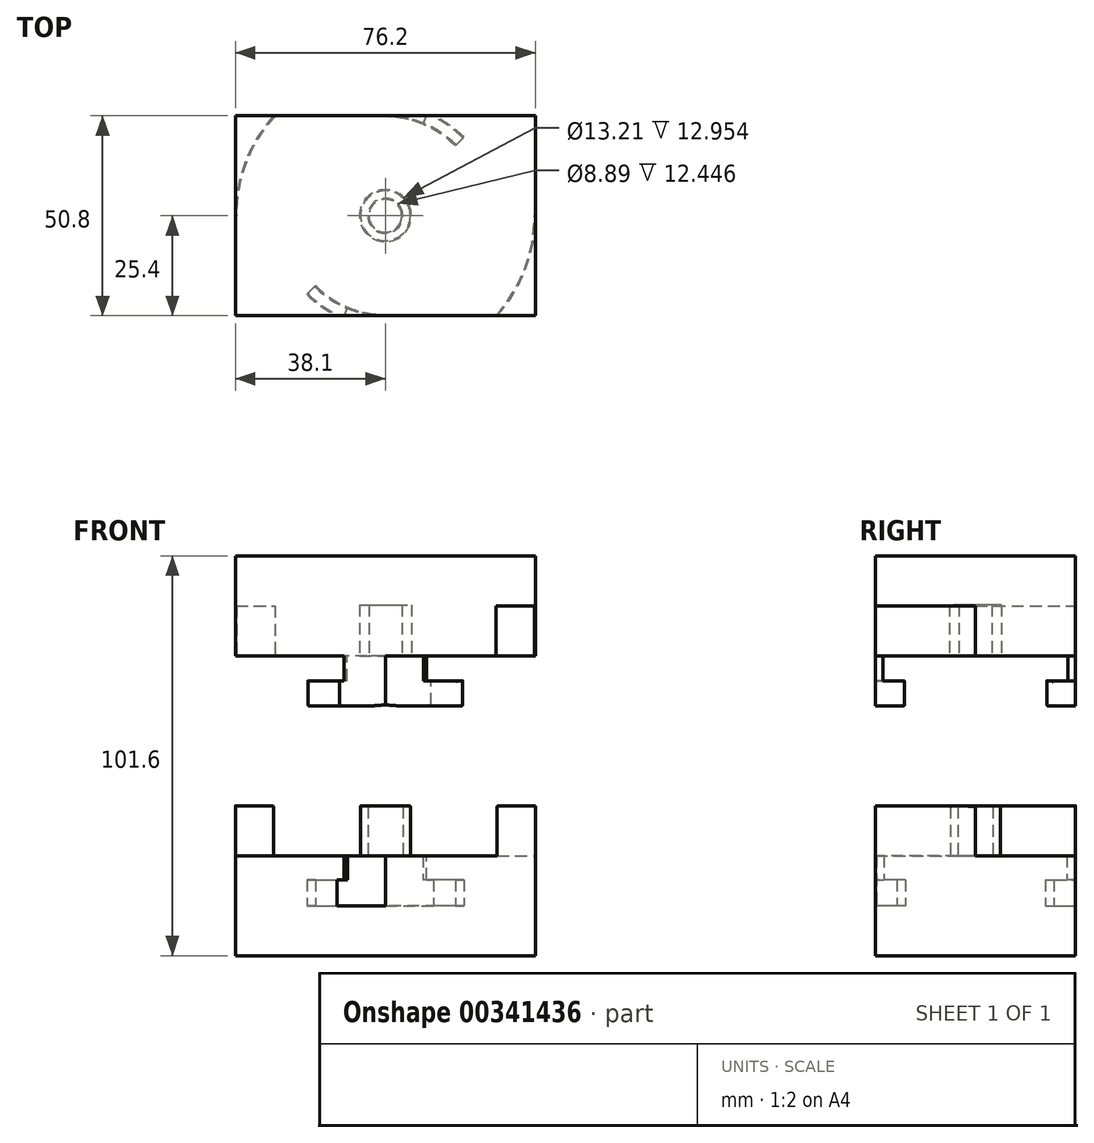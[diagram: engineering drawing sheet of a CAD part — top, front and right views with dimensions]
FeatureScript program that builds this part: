
annotation { "Feature Type Name" : "Feature", "Feature Type Description" : "" }
export const myFeature = defineFeature(function(context is Context, id is Id, definition is map)
    precondition{}
    {
        {
            var Q0;
            Q0=qCreatedBy(makeId("Top.planeOp"),FACE);
            var sketch = newSketch(context, id + "F0", { "sketchPlane" : qUnion([Q0])});
            skLineSegment(sketch, "E0.bottom", {"start": v(-38.1, 25.4) * mm, "end": v(38.1, 25.4) * mm});
            skLineSegment(sketch, "E0.top", {"start": v(-38.1, -25.4) * mm, "end": v(38.1, -25.4) * mm});
            skLineSegment(sketch, "E0.left", {"start": v(-38.1, 25.4) * mm, "end": v(-38.1, -25.4) * mm});
            skLineSegment(sketch, "E0.right", {"start": v(38.1, 25.4) * mm, "end": v(38.1, -25.4) * mm});
            skPoint(sketch, "E0.middle", {"position": v(0, 0) * mm});
            skSolve(sketch);
        }
        {
            var Q0;
            Q0=makeQuery(id+"F0.imprint","IMPRINT",FACE,{"disambiguationData":[TD([[makeQuery(id+"F0.imprint","IMPRINT",EDGE,{"derivedFrom":sQuery(id+"F0.wireOp",EDGE,"E0.bottom")}),-1.0]])]});
            extrude(context, id + "F1", {"entities" : qUnion([Q0]), "depth" : 25.4 * mm});
        }
        {
            var Q0;
            Q0=qCreatedBy(makeId("Top.planeOp"),FACE);
            cPlane(context, id + "F2", {"entities" : qUnion([Q0]), "cplaneType" : CPlaneType.OFFSET, "offset" : 101.6 * mm, "width" : 152.4 * mm, "height" : 152.4 * mm});
        }
        {
            var Q0;
            Q0=qCreatedBy(id+"F2.planeOp",FACE);
            var sketch = newSketch(context, id + "F3", { "sketchPlane" : qUnion([Q0])});
            skLineSegment(sketch, "E1.bottom", {"start": v(-38.1, -25.4) * mm, "end": v(38.1, -25.4) * mm});
            skLineSegment(sketch, "E1.top", {"start": v(-38.1, 25.4) * mm, "end": v(38.1, 25.4) * mm});
            skLineSegment(sketch, "E1.left", {"start": v(-38.1, -25.4) * mm, "end": v(-38.1, 25.4) * mm});
            skLineSegment(sketch, "E1.right", {"start": v(38.1, -25.4) * mm, "end": v(38.1, 25.4) * mm});
            skPoint(sketch, "E1.middle", {"position": v(0, 0) * mm});
            skSolve(sketch);
        }
        {
            var Q0;
            Q0=makeQuery(id+"F3.imprint","IMPRINT",FACE,{"disambiguationData":[TD([[makeQuery(id+"F3.imprint","IMPRINT",EDGE,{"derivedFrom":sQuery(id+"F3.wireOp",EDGE,"E1.bottom")}),1.0]])]});
            extrude(context, id + "F4", {"entities" : qUnion([Q0]), "oppositeDirection" : true, "depth" : 25.4 * mm});
        }
        {
            var Q0;
            Q0=makeQuery(id+"F1.opExtrude","CAP_FACE",FACE,{"disambiguationData":[OSD([sQuery(id+"F0.wireOp",EDGE,"E0.bottom"),sQuery(id+"F0.wireOp",EDGE,"E0.top"),sQuery(id+"F0.wireOp",EDGE,"E0.left"),sQuery(id+"F0.wireOp",EDGE,"E0.right")])],"isStart":false});
            var sketch = newSketch(context, id + "F5", { "sketchPlane" : qUnion([Q0])});
            skCircle(sketch, "E2", {"center": v(0, 0) * mm, "radius": 6.35 * mm});
            skCircle(sketch, "E3", {"center": v(0, 0) * mm, "radius": 4.45 * mm});
            skSolve(sketch);
        }
        {
            var Q0;
            Q0 = qSketchRegion(id + "F5", true);
            extrude(context, id + "F6", {"entities" : qUnion([Q0]), "operationType" : NewBodyOperationType.ADD, "depth" : 12.7 * mm});
        }
        {
            var Q0;
            Q0=makeQuery(id+"F4.opExtrude","CAP_FACE",FACE,{"disambiguationData":[OSD([sQuery(id+"F3.wireOp",EDGE,"E1.bottom"),sQuery(id+"F3.wireOp",EDGE,"E1.top"),sQuery(id+"F3.wireOp",EDGE,"E1.left"),sQuery(id+"F3.wireOp",EDGE,"E1.right")])],"isStart":false});
            var sketch = newSketch(context, id + "F7", { "sketchPlane" : qUnion([Q0])});
            skCircle(sketch, "E4", {"center": v(0, 0) * mm, "radius": 6.6 * mm});
            skCircle(sketch, "E5", {"center": v(0, 0) * mm, "radius": 4.2 * mm});
            skSolve(sketch);
        }
        {
            var Q0;
            Q0 = qSketchRegion(id + "F7", true);
            extrude(context, id + "F8", {"entities" : qUnion([Q0]), "operationType" : NewBodyOperationType.REMOVE, "oppositeDirection" : true, "depth" : 12.95 * mm});
        }
        {
            var Q0;
            Q0=makeQuery(id+"F8.boolean.opBoolean","COPY",EDGE,{"derivedFrom":makeQuery(id+"F8.opExtrude","CAP_EDGE",EDGE,{"disambiguationData":[OSD([sQuery(id+"F7.wireOp",EDGE,"E5")])],"isStart":true})});
            var Q1;
            Q1=makeQuery(id+"F8.boolean.opBoolean","COPY",EDGE,{"derivedFrom":makeQuery(id+"F8.opExtrude","CAP_EDGE",EDGE,{"disambiguationData":[OSD([sQuery(id+"F7.wireOp",EDGE,"E4")])],"isStart":true})});
            fillet(context, id + "F9", {"entities" : qUnion([Q0, Q1]), "radius" : 0.25 * mm, "tangentPropagation" : true, "allowEdgeOverflow" : false});
        }
        {
            var Q0;
            Q0=makeQuery(id+"F6.opExtrude","CAP_EDGE",EDGE,{"disambiguationData":[OSD([sQuery(id+"F5.wireOp",EDGE,"E2")])],"isStart":false});
            var Q1;
            Q1=makeQuery(id+"F6.opExtrude","CAP_EDGE",EDGE,{"disambiguationData":[OSD([sQuery(id+"F5.wireOp",EDGE,"E3")])],"isStart":false});
            fillet(context, id + "F10", {"entities" : qUnion([Q0, Q1]), "radius" : 0.25 * mm, "tangentPropagation" : true, "allowEdgeOverflow" : false});
        }
        {
            var Q0;
            {var subQ0=sQuery(id+"F3.wireOp",EDGE,"E1.left");var subQ1=sQuery(id+"F3.wireOp",EDGE,"E1.top");var subQ2=sQuery(id+"F3.wireOp",EDGE,"E1.right");var subQ3=sQuery(id+"F3.wireOp",EDGE,"E1.bottom");Q0=makeQuery(id+"F8.boolean.opBoolean","SPLIT",FACE,{"disambiguationData":[TD([makeQuery(id+"F4.opExtrude","SWEPT_FACE",FACE,{"disambiguationData":[OSD([subQ3])]})])],"derivedFrom":makeQuery(id+"F4.opExtrude","CAP_FACE",FACE,{"disambiguationData":[OSD([subQ3,subQ1,subQ0,subQ2])],"isStart":false})});}
            var sketch = newSketch(context, id + "F11", { "sketchPlane" : qUnion([Q0])});
            skCircle(sketch, "E6", {"center": v(0, 0) * mm, "radius": 25.4 * mm});
            skCircle(sketch, "E7", {"center": v(0, 0) * mm, "radius": 27.94 * mm});
            skLineSegment(sketch, "E8", {"start": v(-11.64, 25.4) * mm, "end": v(0, 25.4) * mm});
            skLineSegment(sketch, "E9", {"start": v(0, -25.4) * mm, "end": v(11.64, -25.4) * mm});
            skLineSegment(sketch, "E10", {"start": v(-25.4, 0) * mm, "end": v(-27.94, 0) * mm});
            skLineSegment(sketch, "E11", {"start": v(25.4, 0) * mm, "end": v(27.94, 0) * mm});
            skLineSegment(sketch, "E12.1.0", {"start": v(23.47, 9.72) * mm, "end": v(25.81, 10.7) * mm});
            skLineSegment(sketch, "E12.2.0", {"start": v(17.96, 17.96) * mm, "end": v(19.76, 19.76) * mm});
            skLineSegment(sketch, "E13.1.3.0", {"start": v(9.72, 23.47) * mm, "end": v(10.7, 25.81) * mm});
            skLineSegment(sketch, "E13.1.4.0", {"start": v(0, 25.4) * mm, "end": v(0, 27.94) * mm});
            skLineSegment(sketch, "E13.1.5.0", {"start": v(-9.72, 23.47) * mm, "end": v(-10.7, 25.81) * mm});
            skLineSegment(sketch, "E13.1.6.0", {"start": v(-17.96, 17.96) * mm, "end": v(-19.76, 19.76) * mm});
            skLineSegment(sketch, "E13.1.7.0", {"start": v(-23.47, 9.72) * mm, "end": v(-25.81, 10.7) * mm});
            skLineSegment(sketch, "E14.1.9.0", {"start": v(-23.47, -9.72) * mm, "end": v(-25.81, -10.7) * mm});
            skLineSegment(sketch, "E14.1.10.0", {"start": v(-17.96, -17.96) * mm, "end": v(-19.76, -19.76) * mm});
            skLineSegment(sketch, "E14.1.11.0", {"start": v(-9.72, -23.47) * mm, "end": v(-10.7, -25.81) * mm});
            skLineSegment(sketch, "E14.1.12.0", {"start": v(0, -25.4) * mm, "end": v(0, -27.94) * mm});
            skLineSegment(sketch, "E14.1.13.0", {"start": v(9.72, -23.47) * mm, "end": v(10.7, -25.81) * mm});
            skLineSegment(sketch, "E14.1.14.0", {"start": v(17.96, -17.96) * mm, "end": v(19.76, -19.76) * mm});
            skLineSegment(sketch, "E14.1.15.0", {"start": v(23.47, -9.72) * mm, "end": v(25.81, -10.7) * mm});
            skCircle(sketch, "E15", {"center": v(0, 0) * mm, "radius": 37.85 * mm});
            skLineSegment(sketch, "E16", {"start": v(-37.85, 0) * mm, "end": v(-38.1, 0) * mm});
            skLineSegment(sketch, "E17", {"start": v(37.85, 0) * mm, "end": v(38.1, 0) * mm});
            skSolve(sketch);
        }
        {
            var Q0;
            {var subQ0=sQuery(id+"F11.wireOp",EDGE,"E6");var subQ3=sQuery(id+"F11.wireOp",EDGE,"E13.1.5.0");var subQ5=makeQuery(id+"F11.imprint","INTERSECT",VERTEX,{"derivedFrom":[subQ3,subQ0]});Q0=makeQuery(id+"F11.imprint","IMPRINT",FACE,{"disambiguationData":[TD([[makeQuery(id+"F11.imprint","IMPRINT",EDGE,{"disambiguationData":[TD([[subQ5,-1.0]])],"derivedFrom":subQ3}),-1.0]])]});}
            var Q1;
            {var subQ7=sQuery(id+"F11.wireOp",EDGE,"E13.1.6.0");Q1=makeQuery(id+"F11.imprint","IMPRINT",FACE,{"disambiguationData":[TD([[makeQuery(id+"F11.imprint","IMPRINT",EDGE,{"derivedFrom":subQ7}),-1.0]])]});}
            var Q2;
            {var subQ0=sQuery(id+"F11.wireOp",EDGE,"E6");var subQ3=sQuery(id+"F11.wireOp",EDGE,"E14.1.13.0");var subQ5=makeQuery(id+"F11.imprint","INTERSECT",VERTEX,{"derivedFrom":[subQ3,subQ0]});Q2=makeQuery(id+"F11.imprint","IMPRINT",FACE,{"disambiguationData":[TD([[makeQuery(id+"F11.imprint","IMPRINT",EDGE,{"disambiguationData":[TD([[subQ5,-1.0]])],"derivedFrom":subQ3}),-1.0]])]});}
            var Q3;
            {var subQ7=sQuery(id+"F11.wireOp",EDGE,"E14.1.14.0");Q3=makeQuery(id+"F11.imprint","IMPRINT",FACE,{"disambiguationData":[TD([[makeQuery(id+"F11.imprint","IMPRINT",EDGE,{"derivedFrom":subQ7}),-1.0]])]});}
            extrude(context, id + "F12", {"entities" : qUnion([Q0, Q1, Q2, Q3]), "operationType" : NewBodyOperationType.ADD, "depth" : 12.7 * mm});
        }
        {
            var Q0;
            {var subQ7=sQuery(id+"F11.wireOp",EDGE,"E13.1.6.0");Q0=makeQuery(id+"F11.imprint","IMPRINT",FACE,{"disambiguationData":[TD([[makeQuery(id+"F11.imprint","IMPRINT",EDGE,{"derivedFrom":subQ7}),-1.0]])]});}
            var Q1;
            {var subQ7=sQuery(id+"F11.wireOp",EDGE,"E14.1.14.0");Q1=makeQuery(id+"F11.imprint","IMPRINT",FACE,{"disambiguationData":[TD([[makeQuery(id+"F11.imprint","IMPRINT",EDGE,{"derivedFrom":subQ7}),-1.0]])]});}
            extrude(context, id + "F13", {"entities" : qUnion([Q0, Q1]), "operationType" : NewBodyOperationType.REMOVE, "depth" : 6.35 * mm});
        }
        {
            var Q0;
            Q0=qCreatedBy(id+"F2.planeOp",FACE);
            cPlane(context, id + "F14", {"entities" : qUnion([Q0]), "cplaneType" : CPlaneType.OFFSET, "offset" : 88.9 * mm, "oppositeDirection" : true, "width" : 152.4 * mm, "height" : 152.4 * mm});
        }
        {
            var Q0;
            Q0=qCreatedBy(id+"F14.planeOp",FACE);
            var sketch = newSketch(context, id + "F15", { "sketchPlane" : qUnion([Q0])});
            skCircle(sketch, "E18", {"center": v(0, 0) * mm, "radius": 25.15 * mm});
            skCircle(sketch, "E19", {"center": v(0, 0) * mm, "radius": 28.2 * mm});
            skLineSegment(sketch, "E20", {"start": v(0, -25.15) * mm, "end": v(0, -28.2) * mm});
            skLineSegment(sketch, "E21.1.0", {"start": v(9.62, -23.23) * mm, "end": v(10.79, -26.05) * mm});
            skLineSegment(sketch, "E21.2.0", {"start": v(17.78, -17.78) * mm, "end": v(19.94, -19.94) * mm});
            skLineSegment(sketch, "E22.2.3.0", {"start": v(23.23, -9.62) * mm, "end": v(26.05, -10.79) * mm});
            skLineSegment(sketch, "E22.2.4.0", {"start": v(25.15, 0) * mm, "end": v(28.2, 0) * mm});
            skLineSegment(sketch, "E22.2.5.0", {"start": v(23.23, 9.62) * mm, "end": v(26.05, 10.79) * mm});
            skLineSegment(sketch, "E22.2.6.0", {"start": v(17.78, 17.78) * mm, "end": v(19.94, 19.94) * mm});
            skLineSegment(sketch, "E22.2.7.0", {"start": v(9.62, 23.23) * mm, "end": v(10.79, 26.05) * mm});
            skLineSegment(sketch, "E23.2.8.0", {"start": v(0, 25.15) * mm, "end": v(0, 28.2) * mm});
            skLineSegment(sketch, "E23.2.9.0", {"start": v(-9.62, 23.23) * mm, "end": v(-10.79, 26.05) * mm});
            skLineSegment(sketch, "E23.2.10.0", {"start": v(-17.78, 17.78) * mm, "end": v(-19.94, 19.94) * mm});
            skLineSegment(sketch, "E23.2.11.0", {"start": v(-23.23, 9.62) * mm, "end": v(-26.05, 10.79) * mm});
            skLineSegment(sketch, "E23.2.12.0", {"start": v(-25.15, 0) * mm, "end": v(-28.2, 0) * mm});
            skLineSegment(sketch, "E23.2.13.0", {"start": v(-23.23, -9.62) * mm, "end": v(-26.05, -10.79) * mm});
            skLineSegment(sketch, "E23.2.14.0", {"start": v(-17.78, -17.78) * mm, "end": v(-19.94, -19.94) * mm});
            skLineSegment(sketch, "E23.2.15.0", {"start": v(-9.62, -23.23) * mm, "end": v(-10.79, -26.05) * mm});
            skSolve(sketch);
        }
        {
            var Q0;
            {var subQ0=sQuery(id+"F15.wireOp",EDGE,"E20");Q0=makeQuery(id+"F15.imprint","IMPRINT",FACE,{"disambiguationData":[TD([[makeQuery(id+"F15.imprint","IMPRINT",EDGE,{"derivedFrom":subQ0}),-1.0]])]});}
            var Q1;
            {var subQ0=sQuery(id+"F15.wireOp",EDGE,"E23.2.14.0");Q1=makeQuery(id+"F15.imprint","IMPRINT",FACE,{"disambiguationData":[TD([[makeQuery(id+"F15.imprint","IMPRINT",EDGE,{"derivedFrom":subQ0}),1.0]])]});}
            var Q2;
            {var subQ0=sQuery(id+"F15.wireOp",EDGE,"E22.2.7.0");Q2=makeQuery(id+"F15.imprint","IMPRINT",FACE,{"disambiguationData":[TD([[makeQuery(id+"F15.imprint","IMPRINT",EDGE,{"derivedFrom":subQ0}),1.0]])]});}
            var Q3;
            {var subQ0=sQuery(id+"F15.wireOp",EDGE,"E22.2.6.0");Q3=makeQuery(id+"F15.imprint","IMPRINT",FACE,{"disambiguationData":[TD([[makeQuery(id+"F15.imprint","IMPRINT",EDGE,{"derivedFrom":subQ0}),1.0]])]});}
            extrude(context, id + "F16", {"entities" : qUnion([Q0, Q1, Q2, Q3]), "operationType" : NewBodyOperationType.REMOVE, "depth" : 6.6 * mm});
        }
        {
            var Q0;
            {var subQ0=sQuery(id+"F15.wireOp",EDGE,"E20");Q0=makeQuery(id+"F15.imprint","IMPRINT",FACE,{"disambiguationData":[TD([[makeQuery(id+"F15.imprint","IMPRINT",EDGE,{"derivedFrom":subQ0}),-1.0]])]});}
            var Q1;
            {var subQ0=sQuery(id+"F15.wireOp",EDGE,"E22.2.7.0");Q1=makeQuery(id+"F15.imprint","IMPRINT",FACE,{"disambiguationData":[TD([[makeQuery(id+"F15.imprint","IMPRINT",EDGE,{"derivedFrom":subQ0}),1.0]])]});}
            extrude(context, id + "F17", {"entities" : qUnion([Q0, Q1]), "operationType" : NewBodyOperationType.REMOVE, "depth" : 12.7 * mm});
        }
        {
            var Q0;
            {var subQ0=sQuery(id+"F0.wireOp",EDGE,"E0.left");var subQ1=sQuery(id+"F0.wireOp",EDGE,"E0.top");var subQ2=sQuery(id+"F0.wireOp",EDGE,"E0.right");var subQ3=sQuery(id+"F0.wireOp",EDGE,"E0.bottom");Q0=makeQuery(id+"F6.boolean.opBoolean","SPLIT",FACE,{"disambiguationData":[TD([makeQuery(id+"F1.opExtrude","SWEPT_FACE",FACE,{"disambiguationData":[OSD([subQ3])]})])],"derivedFrom":makeQuery(id+"F1.opExtrude","CAP_FACE",FACE,{"disambiguationData":[OSD([subQ3,subQ1,subQ0,subQ2])],"isStart":false})});}
            var sketch = newSketch(context, id + "F18", { "sketchPlane" : qUnion([Q0])});
            skCircle(sketch, "E24", {"center": v(0, 0) * mm, "radius": 38.1 * mm});
            skSolve(sketch);
        }
        {
            var Q0;
            {var subQ0=sQuery(id+"F18.wireOp",EDGE,"E24");var subQ2=sQuery(id+"F0.wireOp",EDGE,"E0.left");var subQ6=makeQuery(id+"F1.opExtrude","CAP_EDGE",EDGE,{"disambiguationData":[OSD([subQ2])],"isStart":false});var subQ7=makeQuery(id+"F18.imprint","INTERSECT",VERTEX,{"derivedFrom":[subQ6,subQ0]});Q0=makeQuery(id+"F18.imprint","IMPRINT",FACE,{"disambiguationData":[TD([[makeQuery(id+"F18.imprint","IMPRINT",EDGE,{"disambiguationData":[TD([[subQ7,1.0]])],"derivedFrom":subQ0}),-1.0]])]});}
            var Q1;
            {var subQ0=sQuery(id+"F18.wireOp",EDGE,"E24");var subQ1=sQuery(id+"F0.wireOp",EDGE,"E0.right");var subQ2=makeQuery(id+"F1.opExtrude","CAP_EDGE",EDGE,{"disambiguationData":[OSD([subQ1])],"isStart":false});var subQ3=makeQuery(id+"F18.imprint","INTERSECT",VERTEX,{"derivedFrom":[subQ2,subQ0]});Q1=makeQuery(id+"F18.imprint","IMPRINT",FACE,{"disambiguationData":[TD([[makeQuery(id+"F18.imprint","IMPRINT",EDGE,{"disambiguationData":[TD([[subQ3,1.0]])],"derivedFrom":subQ0}),-1.0]])]});}
            extrude(context, id + "F19", {"entities" : qUnion([Q0, Q1]), "operationType" : NewBodyOperationType.ADD, "depth" : 12.7 * mm});
        }
        {
            var Q0;
            {var subQ0=sQuery(id+"F11.wireOp",EDGE,"E16");Q0=makeQuery(id+"F11.imprint","IMPRINT",FACE,{"disambiguationData":[TD([[makeQuery(id+"F11.imprint","IMPRINT",EDGE,{"derivedFrom":subQ0}),1.0]])]});}
            var Q1;
            {var subQ0=sQuery(id+"F11.wireOp",EDGE,"E17");Q1=makeQuery(id+"F11.imprint","IMPRINT",FACE,{"disambiguationData":[TD([[makeQuery(id+"F11.imprint","IMPRINT",EDGE,{"derivedFrom":subQ0}),1.0]])]});}
            extrude(context, id + "F20", {"entities" : qUnion([Q0, Q1]), "operationType" : NewBodyOperationType.REMOVE, "oppositeDirection" : true, "depth" : 12.7 * mm});
        }
        {
            var Q0;
            Q0=makeQuery(id+"F12.opExtrude","SWEPT_FACE",FACE,{"disambiguationData":[OSD([sQuery(id+"F11.wireOp",EDGE,"E13.1.6.0")])]});
            var Q1;
            {var subQ0=sQuery(id+"F11.wireOp",EDGE,"E6");var subQ1=makeQuery(id+"F11.imprint","INTERSECT",VERTEX,{"derivedFrom":[sQuery(id+"F11.wireOp",EDGE,"E13.1.5.0"),subQ0]});Q1=makeQuery(id+"F12.opExtrude","CAP_EDGE",EDGE,{"disambiguationData":[OSD([subQ0]),TDD([makeQuery(id+"F11.imprint","IMPRINT",EDGE,{"disambiguationData":[TD([[subQ1,1.0]])],"derivedFrom":subQ0}),makeQuery(id+"F11.imprint","IMPRINT",EDGE,{"disambiguationData":[TD([[subQ1,-1.0]])],"derivedFrom":subQ0})])],"isStart":false});}
            var Q2;
            {var subQ0=sQuery(id+"F11.wireOp",EDGE,"E7");Q2=makeQuery(id+"F12.opExtrude","CAP_EDGE",EDGE,{"disambiguationData":[OSD([subQ0]),TDD([makeQuery(id+"F11.imprint","IMPRINT",EDGE,{"disambiguationData":[TD([[makeQuery(id+"F11.imprint","INTERSECT",VERTEX,{"derivedFrom":[subQ0,sQuery(id+"F11.wireOp",EDGE,"E13.1.6.0")]}),1.0]])],"derivedFrom":subQ0})])],"isStart":false});}
            var Q3;
            {var subQ0=sQuery(id+"F11.wireOp",EDGE,"E6");Q3=makeQuery(id+"F13.boolean.opBoolean","COPY",EDGE,{"derivedFrom":makeQuery(id+"F13.opExtrude","CAP_EDGE",EDGE,{"disambiguationData":[OSD([subQ0]),TDD([makeQuery(id+"F11.imprint","IMPRINT",EDGE,{"disambiguationData":[TD([[makeQuery(id+"F11.imprint","INTERSECT",VERTEX,{"derivedFrom":[sQuery(id+"F11.wireOp",EDGE,"E13.1.5.0"),subQ0]}),-1.0]])],"derivedFrom":subQ0})])],"isStart":false})});}
            var Q4;
            {var subQ0=sQuery(id+"F11.wireOp",EDGE,"E7");Q4=makeQuery(id+"F13.boolean.opBoolean","COPY",EDGE,{"derivedFrom":makeQuery(id+"F13.opExtrude","CAP_EDGE",EDGE,{"disambiguationData":[OSD([subQ0]),TDD([makeQuery(id+"F11.imprint","IMPRINT",EDGE,{"disambiguationData":[TD([[makeQuery(id+"F11.imprint","INTERSECT",VERTEX,{"derivedFrom":[subQ0,sQuery(id+"F11.wireOp",EDGE,"E13.1.6.0")]}),1.0]])],"derivedFrom":subQ0})])],"isStart":false})});}
            var Q5;
            Q5=makeQuery(id+"F13.boolean.opBoolean","COPY",EDGE,{"derivedFrom":makeQuery(id+"F13.opExtrude","SWEPT_EDGE",EDGE,{"disambiguationData":[OSD([sQuery(id+"F11.wireOp",EDGE,"E8"),sQuery(id+"F11.wireOp",EDGE,"E13.1.5.0")])]})});
            var Q6;
            Q6=makeQuery(id+"F13.boolean.opBoolean","COPY",EDGE,{"derivedFrom":makeQuery(id+"F13.opExtrude","SWEPT_EDGE",EDGE,{"disambiguationData":[OSD([sQuery(id+"F11.wireOp",EDGE,"E13.1.5.0"),sQuery(id+"F11.wireOp",EDGE,"E6")])]})});
            var Q7;
            Q7=makeQuery(id+"F12.opExtrude","SWEPT_FACE",FACE,{"disambiguationData":[OSD([sQuery(id+"F11.wireOp",EDGE,"E14.1.14.0")])]});
            var Q8;
            {var subQ0=sQuery(id+"F11.wireOp",EDGE,"E6");Q8=makeQuery(id+"F13.boolean.opBoolean","COPY",EDGE,{"derivedFrom":makeQuery(id+"F13.opExtrude","CAP_EDGE",EDGE,{"disambiguationData":[OSD([subQ0]),TDD([makeQuery(id+"F11.imprint","IMPRINT",EDGE,{"disambiguationData":[TD([[makeQuery(id+"F11.imprint","INTERSECT",VERTEX,{"derivedFrom":[sQuery(id+"F11.wireOp",EDGE,"E14.1.13.0"),subQ0]}),-1.0]])],"derivedFrom":subQ0})])],"isStart":false})});}
            var Q9;
            {var subQ0=sQuery(id+"F11.wireOp",EDGE,"E7");Q9=makeQuery(id+"F13.boolean.opBoolean","COPY",EDGE,{"derivedFrom":makeQuery(id+"F13.opExtrude","CAP_EDGE",EDGE,{"disambiguationData":[OSD([subQ0]),TDD([makeQuery(id+"F11.imprint","IMPRINT",EDGE,{"disambiguationData":[TD([[makeQuery(id+"F11.imprint","INTERSECT",VERTEX,{"derivedFrom":[subQ0,sQuery(id+"F11.wireOp",EDGE,"E14.1.14.0")]}),1.0]])],"derivedFrom":subQ0})])],"isStart":false})});}
            var Q10;
            {var subQ0=sQuery(id+"F11.wireOp",EDGE,"E7");Q10=makeQuery(id+"F12.opExtrude","CAP_EDGE",EDGE,{"disambiguationData":[OSD([subQ0]),TDD([makeQuery(id+"F11.imprint","IMPRINT",EDGE,{"disambiguationData":[TD([[makeQuery(id+"F11.imprint","INTERSECT",VERTEX,{"derivedFrom":[subQ0,sQuery(id+"F11.wireOp",EDGE,"E14.1.14.0")]}),1.0]])],"derivedFrom":subQ0})])],"isStart":false});}
            var Q11;
            {var subQ0=sQuery(id+"F11.wireOp",EDGE,"E6");var subQ1=makeQuery(id+"F11.imprint","INTERSECT",VERTEX,{"derivedFrom":[sQuery(id+"F11.wireOp",EDGE,"E14.1.13.0"),subQ0]});Q11=makeQuery(id+"F12.opExtrude","CAP_EDGE",EDGE,{"disambiguationData":[OSD([subQ0]),TDD([makeQuery(id+"F11.imprint","IMPRINT",EDGE,{"disambiguationData":[TD([[subQ1,1.0]])],"derivedFrom":subQ0}),makeQuery(id+"F11.imprint","IMPRINT",EDGE,{"disambiguationData":[TD([[subQ1,-1.0]])],"derivedFrom":subQ0})])],"isStart":false});}
            var Q12;
            Q12=makeQuery(id+"F13.boolean.opBoolean","COPY",EDGE,{"derivedFrom":makeQuery(id+"F13.opExtrude","SWEPT_EDGE",EDGE,{"disambiguationData":[OSD([sQuery(id+"F11.wireOp",EDGE,"E9"),sQuery(id+"F11.wireOp",EDGE,"E14.1.13.0")])]})});
            var Q13;
            Q13=makeQuery(id+"F13.boolean.opBoolean","COPY",EDGE,{"derivedFrom":makeQuery(id+"F13.opExtrude","SWEPT_EDGE",EDGE,{"disambiguationData":[OSD([sQuery(id+"F11.wireOp",EDGE,"E14.1.13.0"),sQuery(id+"F11.wireOp",EDGE,"E6")])]})});
            fillet(context, id + "F21", {"entities" : qUnion([Q0, Q1, Q2, Q3, Q4, Q5, Q6, Q7, Q8, Q9, Q10, Q11, Q12, Q13]), "radius" : 0.25 * mm, "tangentPropagation" : true, "allowEdgeOverflow" : false});
        }
        {
            var Q0;
            {var subQ0=sQuery(id+"F18.wireOp",EDGE,"E24");var subQ2=sQuery(id+"F0.wireOp",EDGE,"E0.left");Q0=makeQuery(id+"F19.opExtrude","CAP_EDGE",EDGE,{"disambiguationData":[OSD([subQ0]),TDD([makeQuery(id+"F18.imprint","IMPRINT",EDGE,{"disambiguationData":[TD([[makeQuery(id+"F18.imprint","INTERSECT",VERTEX,{"derivedFrom":[makeQuery(id+"F1.opExtrude","CAP_EDGE",EDGE,{"disambiguationData":[OSD([subQ2])],"isStart":false}),subQ0]}),1.0]])],"derivedFrom":subQ0})])],"isStart":false});}
            var Q1;
            {var subQ0=sQuery(id+"F18.wireOp",EDGE,"E24");var subQ1=sQuery(id+"F0.wireOp",EDGE,"E0.right");Q1=makeQuery(id+"F19.opExtrude","CAP_EDGE",EDGE,{"disambiguationData":[OSD([subQ0]),TDD([makeQuery(id+"F18.imprint","IMPRINT",EDGE,{"disambiguationData":[TD([[makeQuery(id+"F18.imprint","INTERSECT",VERTEX,{"derivedFrom":[makeQuery(id+"F1.opExtrude","CAP_EDGE",EDGE,{"disambiguationData":[OSD([subQ1])],"isStart":false}),subQ0]}),1.0]])],"derivedFrom":subQ0})])],"isStart":false});}
            var Q2;
            Q2=makeQuery(id+"F20.boolean.opBoolean","COPY",EDGE,{"derivedFrom":makeQuery(id+"F20.opExtrude","SWEPT_EDGE",EDGE,{"disambiguationData":[OSD([sQuery(id+"F3.wireOp",EDGE,"E1.top"),sQuery(id+"F11.wireOp",EDGE,"E15")])]})});
            var Q3;
            Q3=makeQuery(id+"F20.boolean.opBoolean","COPY",EDGE,{"derivedFrom":makeQuery(id+"F20.opExtrude","SWEPT_EDGE",EDGE,{"disambiguationData":[OSD([sQuery(id+"F3.wireOp",EDGE,"E1.bottom"),sQuery(id+"F11.wireOp",EDGE,"E15")])]})});
            fillet(context, id + "F22", {"entities" : qUnion([Q0, Q1, Q2, Q3]), "radius" : 0.25 * mm, "tangentPropagation" : true, "allowEdgeOverflow" : false});
        }
    });
